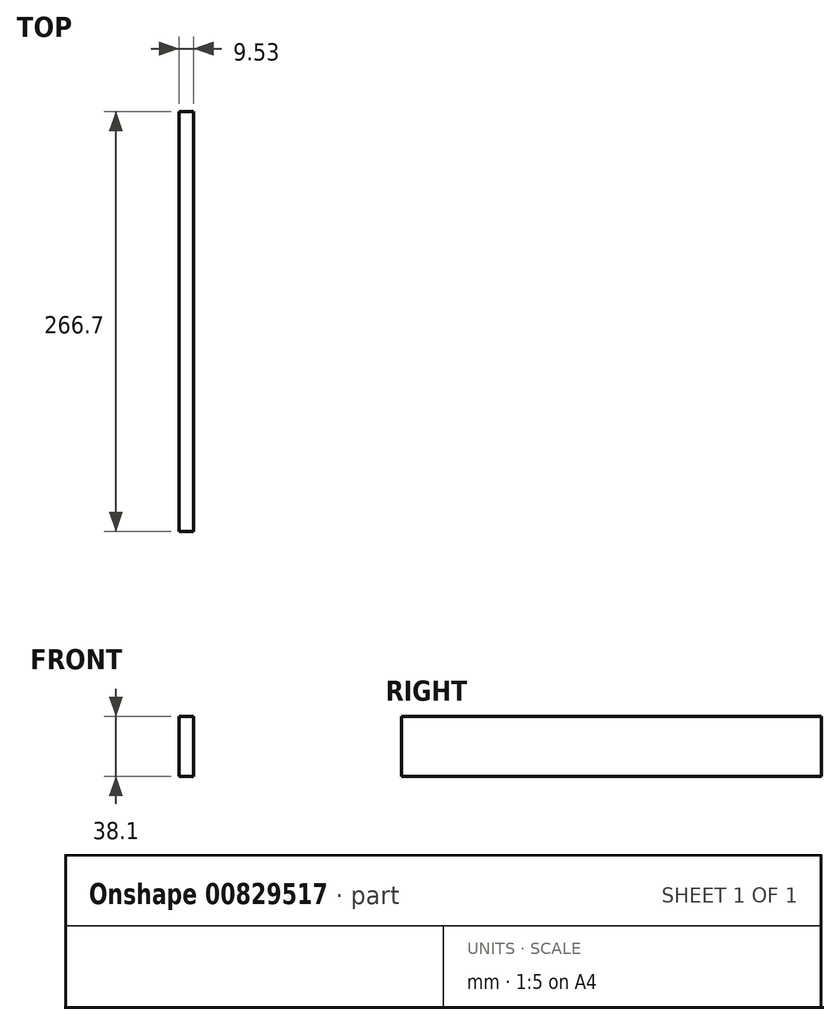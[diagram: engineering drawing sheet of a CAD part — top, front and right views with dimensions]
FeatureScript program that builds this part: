
annotation { "Feature Type Name" : "Feature", "Feature Type Description" : "" }
export const myFeature = defineFeature(function(context is Context, id is Id, definition is map)
    precondition{}
    {
        {
            var Q0;
            Q0=qCreatedBy(makeId("Right.planeOp"),FACE);
            var sketch = newSketch(context, id + "F0", { "sketchPlane" : qUnion([Q0])});
            skLineSegment(sketch, "E0.bottom", {"start": v(-133.35, -19.05) * mm, "end": v(133.35, -19.05) * mm});
            skLineSegment(sketch, "E0.top", {"start": v(-133.35, 19.05) * mm, "end": v(133.35, 19.05) * mm});
            skLineSegment(sketch, "E0.left", {"start": v(-133.35, -19.05) * mm, "end": v(-133.35, 19.05) * mm});
            skLineSegment(sketch, "E0.right", {"start": v(133.35, -19.05) * mm, "end": v(133.35, 19.05) * mm});
            skPoint(sketch, "E0.middle", {"position": v(0, 0) * mm});
            skSolve(sketch);
        }
        {
            var Q0;
            Q0 = qSketchRegion(id + "F0", true);
            extrude(context, id + "F1", {"entities" : qUnion([Q0]), "depth" : 9.52 * mm, "offsetDistance" : 25.4 * mm});
        }
    });
